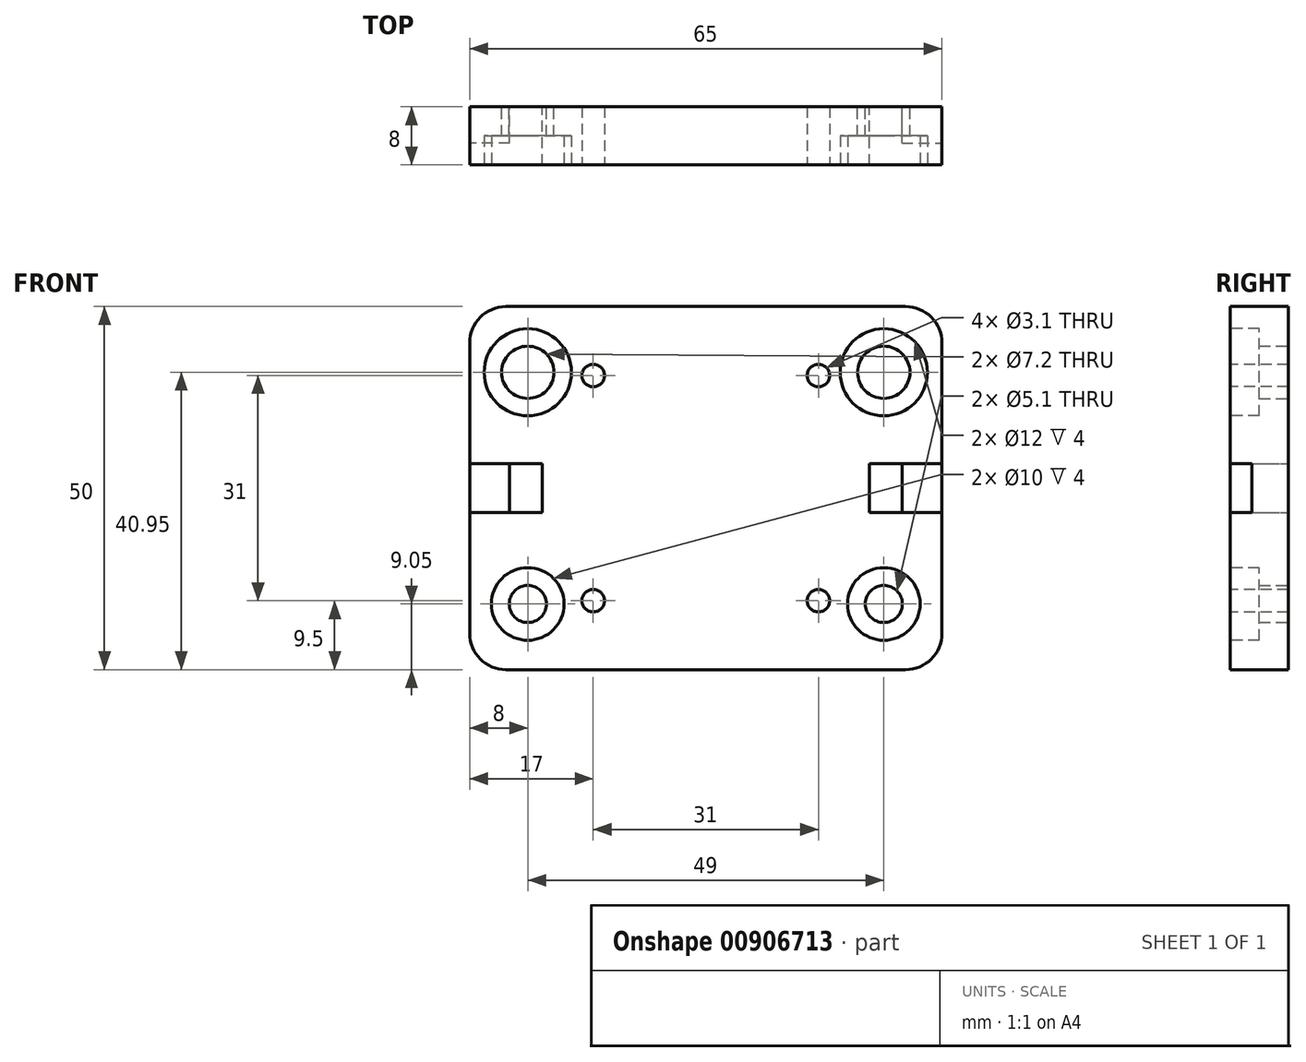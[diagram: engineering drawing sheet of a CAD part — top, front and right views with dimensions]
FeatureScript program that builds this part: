
annotation { "Feature Type Name" : "Feature", "Feature Type Description" : "" }
export const myFeature = defineFeature(function(context is Context, id is Id, definition is map)
    precondition{}
    {
        {
            var Q0;
            Q0=qCreatedBy(makeId("Front.planeOp"),FACE);
            var sketch = newSketch(context, id + "F0", { "sketchPlane" : qUnion([Q0])});
            skLineSegment(sketch, "E0.bottom", {"start": v(-32.5, 25) * mm, "end": v(32.5, 25) * mm});
            skLineSegment(sketch, "E0.top", {"start": v(-32.5, -25) * mm, "end": v(32.5, -25) * mm});
            skLineSegment(sketch, "E0.left", {"start": v(-32.5, 25) * mm, "end": v(-32.5, -25) * mm});
            skLineSegment(sketch, "E0.right", {"start": v(32.5, 25) * mm, "end": v(32.5, -25) * mm});
            skPoint(sketch, "E0.middle", {"position": v(0, 0) * mm});
            skLineSegment(sketch, "E1.bottom", {"start": v(-24.5, 15.95) * mm, "end": v(24.5, 15.95) * mm});
            skLineSegment(sketch, "E1.top", {"start": v(-24.5, -15.95) * mm, "end": v(24.5, -15.95) * mm});
            skLineSegment(sketch, "E1.left", {"start": v(-24.5, 15.95) * mm, "end": v(-24.5, -15.95) * mm});
            skLineSegment(sketch, "E1.right", {"start": v(24.5, 15.95) * mm, "end": v(24.5, -15.95) * mm});
            skCircle(sketch, "E2", {"center": v(-24.5, 15.95) * mm, "radius": 3.6 * mm});
            skCircle(sketch, "E3", {"center": v(24.5, 15.95) * mm, "radius": 3.6 * mm});
            skCircle(sketch, "E4", {"center": v(-24.5, -15.95) * mm, "radius": 2.55 * mm});
            skCircle(sketch, "E5", {"center": v(24.5, -15.95) * mm, "radius": 2.55 * mm});
            skLineSegment(sketch, "E6.bottom", {"start": v(-22.5, 3.35) * mm, "end": v(22.5, 3.35) * mm});
            skLineSegment(sketch, "E6.top", {"start": v(-22.5, -3.35) * mm, "end": v(22.5, -3.35) * mm});
            skLineSegment(sketch, "E6.left", {"start": v(-22.5, 3.35) * mm, "end": v(-22.5, -3.35) * mm});
            skLineSegment(sketch, "E6.right", {"start": v(22.5, 3.35) * mm, "end": v(22.5, -3.35) * mm});
            skLineSegment(sketch, "E7.bottom", {"start": v(-27, 3.35) * mm, "end": v(27, 3.35) * mm});
            skLineSegment(sketch, "E7.top", {"start": v(-27, -3.35) * mm, "end": v(27, -3.35) * mm});
            skLineSegment(sketch, "E7.left", {"start": v(-27, 3.35) * mm, "end": v(-27, -3.35) * mm});
            skLineSegment(sketch, "E7.right", {"start": v(27, 3.35) * mm, "end": v(27, -3.35) * mm});
            skSolve(sketch);
        }
        {
            var Q0;
            Q0=qSketchRegion(id+"F0",true);
            var Q1;
            {var subQ0=sQuery(id+"F0.wireOp",EDGE,"E2");var subQ1=sQuery(id+"F0.wireOp",EDGE,"E1.bottom");var subQ2=makeQuery(id+"F0.imprint","INTERSECT",VERTEX,{"derivedFrom":[subQ1,subQ0]});Q1=makeQuery(id+"F0.imprint","IMPRINT",FACE,{"disambiguationData":[TD([[makeQuery(id+"F0.imprint","IMPRINT",EDGE,{"disambiguationData":[TD([[subQ2,-1.0]])],"derivedFrom":subQ1}),-1.0]])]});}
            var Q2;
            {var subQ0=sQuery(id+"F0.wireOp",EDGE,"E4");var subQ1=sQuery(id+"F0.wireOp",EDGE,"E1.top");var subQ2=makeQuery(id+"F0.imprint","INTERSECT",VERTEX,{"derivedFrom":[subQ1,subQ0]});Q2=makeQuery(id+"F0.imprint","IMPRINT",FACE,{"disambiguationData":[TD([[makeQuery(id+"F0.imprint","IMPRINT",EDGE,{"disambiguationData":[TD([[subQ2,-1.0]])],"derivedFrom":subQ1}),1.0]])]});}
            var Q3;
            {var subQ5=sQuery(id+"F0.wireOp",EDGE,"E6.left");Q3=makeQuery(id+"F0.imprint","IMPRINT",FACE,{"disambiguationData":[TD([[makeQuery(id+"F0.imprint","IMPRINT",EDGE,{"derivedFrom":subQ5}),1.0]])]});}
            var Q4;
            {var subQ5=sQuery(id+"F0.wireOp",EDGE,"E6.right");Q4=makeQuery(id+"F0.imprint","IMPRINT",FACE,{"disambiguationData":[TD([[makeQuery(id+"F0.imprint","IMPRINT",EDGE,{"derivedFrom":subQ5}),-1.0]])]});}
            extrude(context, id + "F1", {"entities" : qUnion([Q0, Q1, Q2, Q3, Q4]), "depth" : 8 * mm, "offsetDistance" : 25 * mm});
        }
        {
            var Q0;
            Q0=makeQuery(id+"F1.opExtrude","CAP_FACE",FACE,{"disambiguationData":[OSD([sQuery(id+"F0.wireOp",EDGE,"E0.bottom"),sQuery(id+"F0.wireOp",EDGE,"E0.top"),sQuery(id+"F0.wireOp",EDGE,"E0.left"),sQuery(id+"F0.wireOp",EDGE,"E0.right"),sQuery(id+"F0.wireOp",EDGE,"E2"),sQuery(id+"F0.wireOp",EDGE,"E3"),sQuery(id+"F0.wireOp",EDGE,"E4"),sQuery(id+"F0.wireOp",EDGE,"E5"),sQuery(id+"F0.wireOp",EDGE,"E6.left"),sQuery(id+"F0.wireOp",EDGE,"E6.right"),sQuery(id+"F0.wireOp",EDGE,"E7.bottom"),sQuery(id+"F0.wireOp",EDGE,"E7.top"),sQuery(id+"F0.wireOp",EDGE,"E7.left"),sQuery(id+"F0.wireOp",EDGE,"E7.right")])],"isStart":false});
            var sketch = newSketch(context, id + "F2", { "sketchPlane" : qUnion([Q0])});
            skCircle(sketch, "E8", {"center": v(-24.5, 15.95) * mm, "radius": 6 * mm});
            skCircle(sketch, "E9", {"center": v(24.5, 15.95) * mm, "radius": 6 * mm});
            skCircle(sketch, "E10", {"center": v(-24.5, -15.95) * mm, "radius": 5 * mm});
            skCircle(sketch, "E11", {"center": v(24.5, -15.95) * mm, "radius": 5 * mm});
            skSolve(sketch);
        }
        {
            var Q0;
            Q0=makeQuery(id+"F2.imprint","IMPRINT",FACE,{"disambiguationData":[TD([[makeQuery(id+"F2.imprint","IMPRINT",EDGE,{"derivedFrom":sQuery(id+"F2.wireOp",EDGE,"E9")}),1.0]])]});
            var Q1;
            Q1=makeQuery(id+"F2.imprint","IMPRINT",FACE,{"disambiguationData":[TD([[makeQuery(id+"F2.imprint","IMPRINT",EDGE,{"derivedFrom":sQuery(id+"F2.wireOp",EDGE,"E8")}),1.0]])]});
            var Q2;
            Q2=makeQuery(id+"F2.imprint","IMPRINT",FACE,{"disambiguationData":[TD([[makeQuery(id+"F2.imprint","IMPRINT",EDGE,{"derivedFrom":sQuery(id+"F2.wireOp",EDGE,"E10")}),1.0]])]});
            var Q3;
            Q3=makeQuery(id+"F2.imprint","IMPRINT",FACE,{"disambiguationData":[TD([[makeQuery(id+"F2.imprint","IMPRINT",EDGE,{"derivedFrom":sQuery(id+"F2.wireOp",EDGE,"E11")}),1.0]])]});
            extrude(context, id + "F3", {"entities" : qUnion([Q0, Q1, Q2, Q3]), "operationType" : NewBodyOperationType.REMOVE, "oppositeDirection" : true, "depth" : 4 * mm, "offsetDistance" : 25 * mm});
        }
        {
            var Q0;
            Q0=makeQuery(id+"F1.opExtrude","CAP_FACE",FACE,{"disambiguationData":[OSD([sQuery(id+"F0.wireOp",EDGE,"E0.bottom"),sQuery(id+"F0.wireOp",EDGE,"E0.top"),sQuery(id+"F0.wireOp",EDGE,"E0.left"),sQuery(id+"F0.wireOp",EDGE,"E0.right"),sQuery(id+"F0.wireOp",EDGE,"E2"),sQuery(id+"F0.wireOp",EDGE,"E3"),sQuery(id+"F0.wireOp",EDGE,"E4"),sQuery(id+"F0.wireOp",EDGE,"E5"),sQuery(id+"F0.wireOp",EDGE,"E6.left"),sQuery(id+"F0.wireOp",EDGE,"E6.right"),sQuery(id+"F0.wireOp",EDGE,"E7.bottom"),sQuery(id+"F0.wireOp",EDGE,"E7.top"),sQuery(id+"F0.wireOp",EDGE,"E7.left"),sQuery(id+"F0.wireOp",EDGE,"E7.right")])],"isStart":false});
            var sketch = newSketch(context, id + "F4", { "sketchPlane" : qUnion([Q0])});
            skLineSegment(sketch, "E12.bottom", {"start": v(27, 3.35) * mm, "end": v(32.5, 3.35) * mm});
            skLineSegment(sketch, "E12.top", {"start": v(27, -3.35) * mm, "end": v(32.5, -3.35) * mm});
            skLineSegment(sketch, "E12.left", {"start": v(27, 3.35) * mm, "end": v(27, -3.35) * mm});
            skLineSegment(sketch, "E12.right", {"start": v(32.5, 3.35) * mm, "end": v(32.5, -3.35) * mm});
            skLineSegment(sketch, "E13.bottom", {"start": v(-27, 3.35) * mm, "end": v(-32.5, 3.35) * mm});
            skLineSegment(sketch, "E13.top", {"start": v(-27, -3.35) * mm, "end": v(-32.5, -3.35) * mm});
            skLineSegment(sketch, "E13.left", {"start": v(-27, 3.35) * mm, "end": v(-27, -3.35) * mm});
            skLineSegment(sketch, "E13.right", {"start": v(-32.5, 3.35) * mm, "end": v(-32.5, -3.35) * mm});
            skSolve(sketch);
        }
        {
            var Q0;
            Q0=qSketchRegion(id+"F4",true);
            extrude(context, id + "F5", {"entities" : qUnion([Q0]), "operationType" : NewBodyOperationType.REMOVE, "oppositeDirection" : true, "depth" : 3 * mm, "offsetDistance" : 25 * mm});
        }
        {
            var Q0;
            Q0=makeQuery(id+"F1.opExtrude","SWEPT_EDGE",EDGE,{"disambiguationData":[OSD([sQuery(id+"F0.wireOp",EDGE,"E0.bottom"),sQuery(id+"F0.wireOp",EDGE,"E0.left")])]});
            var Q1;
            Q1=makeQuery(id+"F1.opExtrude","SWEPT_EDGE",EDGE,{"disambiguationData":[OSD([sQuery(id+"F0.wireOp",EDGE,"E0.bottom"),sQuery(id+"F0.wireOp",EDGE,"E0.right")])]});
            var Q2;
            Q2=makeQuery(id+"F1.opExtrude","SWEPT_EDGE",EDGE,{"disambiguationData":[OSD([sQuery(id+"F0.wireOp",EDGE,"E0.top"),sQuery(id+"F0.wireOp",EDGE,"E0.right")])]});
            var Q3;
            Q3=makeQuery(id+"F1.opExtrude","SWEPT_EDGE",EDGE,{"disambiguationData":[OSD([sQuery(id+"F0.wireOp",EDGE,"E0.top"),sQuery(id+"F0.wireOp",EDGE,"E0.left")])]});
            fillet(context, id + "F6", {"entities" : qUnion([Q0, Q1, Q2, Q3]), "radius" : 5 * mm, "tangentPropagation" : true, "allowEdgeOverflow" : false});
        }
        {
            var Q0;
            Q0=makeQuery(id+"F1.opExtrude","CAP_FACE",FACE,{"disambiguationData":[OSD([sQuery(id+"F0.wireOp",EDGE,"E0.bottom"),sQuery(id+"F0.wireOp",EDGE,"E0.top"),sQuery(id+"F0.wireOp",EDGE,"E0.left"),sQuery(id+"F0.wireOp",EDGE,"E0.right"),sQuery(id+"F0.wireOp",EDGE,"E2"),sQuery(id+"F0.wireOp",EDGE,"E3"),sQuery(id+"F0.wireOp",EDGE,"E4"),sQuery(id+"F0.wireOp",EDGE,"E5"),sQuery(id+"F0.wireOp",EDGE,"E6.left"),sQuery(id+"F0.wireOp",EDGE,"E6.right"),sQuery(id+"F0.wireOp",EDGE,"E7.bottom"),sQuery(id+"F0.wireOp",EDGE,"E7.top"),sQuery(id+"F0.wireOp",EDGE,"E7.left"),sQuery(id+"F0.wireOp",EDGE,"E7.right")])],"isStart":false});
            var sketch = newSketch(context, id + "F7", { "sketchPlane" : qUnion([Q0])});
            skLineSegment(sketch, "E14.bottom", {"start": v(-15.5, 15.5) * mm, "end": v(15.5, 15.5) * mm});
            skLineSegment(sketch, "E14.top", {"start": v(-15.5, -15.5) * mm, "end": v(15.5, -15.5) * mm});
            skLineSegment(sketch, "E14.left", {"start": v(-15.5, 15.5) * mm, "end": v(-15.5, -15.5) * mm});
            skLineSegment(sketch, "E14.right", {"start": v(15.5, 15.5) * mm, "end": v(15.5, -15.5) * mm});
            skPoint(sketch, "E14.middle", {"position": v(0, 0) * mm});
            skPoint(sketch, "E14.middle.positionSnap0", {"position": v(22.5, 0) * mm});
            skPoint(sketch, "E14.middle.positionSnap1", {"position": v(0, 25) * mm});
            skPoint(sketch, "E14.centerSnap0", {"position": v(22.5, 0) * mm});
            skPoint(sketch, "E14.centerSnap1", {"position": v(0, 25) * mm});
            skCircle(sketch, "E15", {"center": v(-15.5, 15.5) * mm, "radius": 1.55 * mm});
            skCircle(sketch, "E16", {"center": v(15.5, 15.5) * mm, "radius": 1.55 * mm});
            skCircle(sketch, "E17", {"center": v(-15.5, -15.5) * mm, "radius": 1.55 * mm});
            skCircle(sketch, "E18", {"center": v(15.5, -15.5) * mm, "radius": 1.55 * mm});
            skSolve(sketch);
        }
        {
            var Q0;
            {var subQ0=sQuery(id+"F7.wireOp",EDGE,"E14.left");var subQ1=sQuery(id+"F7.wireOp",EDGE,"E14.bottom");var subQ2=makeQuery(id+"F7.imprint","INTERSECT",VERTEX,{"derivedFrom":[subQ1,subQ0]});Q0=makeQuery(id+"F7.imprint","IMPRINT",FACE,{"disambiguationData":[TD([[makeQuery(id+"F7.imprint","IMPRINT",EDGE,{"disambiguationData":[TD([[subQ2,-1.0]])],"derivedFrom":subQ1}),1.0]])]});}
            var Q1;
            {var subQ0=sQuery(id+"F7.wireOp",EDGE,"E14.left");var subQ1=sQuery(id+"F7.wireOp",EDGE,"E14.bottom");var subQ2=makeQuery(id+"F7.imprint","INTERSECT",VERTEX,{"derivedFrom":[subQ1,subQ0]});Q1=makeQuery(id+"F7.imprint","IMPRINT",FACE,{"disambiguationData":[TD([[makeQuery(id+"F7.imprint","IMPRINT",EDGE,{"disambiguationData":[TD([[subQ2,-1.0]])],"derivedFrom":subQ1}),-1.0]])]});}
            var Q2;
            {var subQ0=sQuery(id+"F7.wireOp",EDGE,"E14.left");var subQ1=sQuery(id+"F7.wireOp",EDGE,"E14.top");var subQ2=makeQuery(id+"F7.imprint","INTERSECT",VERTEX,{"derivedFrom":[subQ1,subQ0]});Q2=makeQuery(id+"F7.imprint","IMPRINT",FACE,{"disambiguationData":[TD([[makeQuery(id+"F7.imprint","IMPRINT",EDGE,{"disambiguationData":[TD([[subQ2,-1.0]])],"derivedFrom":subQ1}),1.0]])]});}
            var Q3;
            {var subQ0=sQuery(id+"F7.wireOp",EDGE,"E14.left");var subQ1=sQuery(id+"F7.wireOp",EDGE,"E14.top");var subQ2=makeQuery(id+"F7.imprint","INTERSECT",VERTEX,{"derivedFrom":[subQ1,subQ0]});Q3=makeQuery(id+"F7.imprint","IMPRINT",FACE,{"disambiguationData":[TD([[makeQuery(id+"F7.imprint","IMPRINT",EDGE,{"disambiguationData":[TD([[subQ2,-1.0]])],"derivedFrom":subQ1}),-1.0]])]});}
            var Q4;
            {var subQ0=sQuery(id+"F7.wireOp",EDGE,"E14.right");var subQ1=sQuery(id+"F7.wireOp",EDGE,"E14.top");var subQ2=makeQuery(id+"F7.imprint","INTERSECT",VERTEX,{"derivedFrom":[subQ1,subQ0]});Q4=makeQuery(id+"F7.imprint","IMPRINT",FACE,{"disambiguationData":[TD([[makeQuery(id+"F7.imprint","IMPRINT",EDGE,{"disambiguationData":[TD([[subQ2,1.0]])],"derivedFrom":subQ1}),1.0]])]});}
            var Q5;
            {var subQ0=sQuery(id+"F7.wireOp",EDGE,"E14.right");var subQ1=sQuery(id+"F7.wireOp",EDGE,"E14.top");var subQ2=makeQuery(id+"F7.imprint","INTERSECT",VERTEX,{"derivedFrom":[subQ1,subQ0]});Q5=makeQuery(id+"F7.imprint","IMPRINT",FACE,{"disambiguationData":[TD([[makeQuery(id+"F7.imprint","IMPRINT",EDGE,{"disambiguationData":[TD([[subQ2,1.0]])],"derivedFrom":subQ1}),-1.0]])]});}
            var Q6;
            {var subQ0=sQuery(id+"F7.wireOp",EDGE,"E14.right");var subQ1=sQuery(id+"F7.wireOp",EDGE,"E14.bottom");var subQ2=makeQuery(id+"F7.imprint","INTERSECT",VERTEX,{"derivedFrom":[subQ1,subQ0]});Q6=makeQuery(id+"F7.imprint","IMPRINT",FACE,{"disambiguationData":[TD([[makeQuery(id+"F7.imprint","IMPRINT",EDGE,{"disambiguationData":[TD([[subQ2,1.0]])],"derivedFrom":subQ1}),-1.0]])]});}
            var Q7;
            {var subQ0=sQuery(id+"F7.wireOp",EDGE,"E14.right");var subQ1=sQuery(id+"F7.wireOp",EDGE,"E14.bottom");var subQ2=makeQuery(id+"F7.imprint","INTERSECT",VERTEX,{"derivedFrom":[subQ1,subQ0]});Q7=makeQuery(id+"F7.imprint","IMPRINT",FACE,{"disambiguationData":[TD([[makeQuery(id+"F7.imprint","IMPRINT",EDGE,{"disambiguationData":[TD([[subQ2,1.0]])],"derivedFrom":subQ1}),1.0]])]});}
            extrude(context, id + "F8", {"entities" : qUnion([Q0, Q1, Q2, Q3, Q4, Q5, Q6, Q7]), "operationType" : NewBodyOperationType.REMOVE, "oppositeDirection" : true, "depth" : 25 * mm, "offsetDistance" : 25 * mm});
        }
    });
